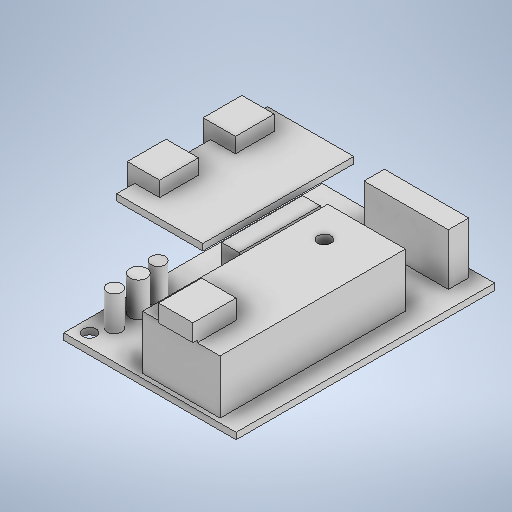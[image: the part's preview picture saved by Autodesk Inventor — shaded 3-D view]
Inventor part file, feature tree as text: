
AUTODESK INVENTOR PART (.ipt)
format: ipt  version: 2025.1 (Build 291241000, 241)  size: 356,864 bytes
history: native  units: mm
features: sketch x10, extrude x9, plane x2, hole x1
ambient origin geometry x8: Origin, YZ Plane, XZ Plane, XY Plane, X Axis, Y Axis, Z Axis, Center Point
bodies: Volumenkörper1 (feature_tree)
feature tree (22):
  extrude  "Extrusion1"  Depth=60.0mm
  extrude  "Extrusion2"  Depth=8.0mm
  extrude  "Extrusion3"  Depth=10.0mm
  plane  "Arbeitsebene1"
  extrude  "Extrusion4"  Depth=4.0mm
  extrude  "Extrusion5"  Depth=35.0mm
  extrude  "Extrusion6"  Depth=3.7mm
  extrude  "Extrusion7"  Depth=11.3mm
  extrude  "Extrusion8"  Depth=7.5mm
  extrude  "Extrusion9"  Depth=1.75mm
  plane  "Arbeitsebene2"
  hole  "Bohrung1"  [1 undecoded]
  sketch  "Skizze1"  dims[d0=40.0mm d1=60.0mm]
  sketch  "Skizze2"  dims[d2=1.5mm d3=0.0mm d4=8.0mm]
  sketch  "Skizze3"  dims[d5=10.0mm d6=10.0mm]
  sketch  "Skizze4"  dims[d7=17.0mm d8=0.0mm d9=4.0mm]
  sketch  "Skizze5"  dims[d10=1.0mm d11=0.0mm d12=35.0mm]
  sketch  "Skizze6"  dims[d13=20.0mm d14=3.7mm]
  sketch  "Skizze7"  dims[d15=29.0mm d16=11.3mm]
  sketch  "Skizze8"  dims[d17=1.5mm d18=0.0mm d19=7.5mm]
  sketch  "Skizze9"  dims[d20=9.0mm d21=1.75mm]
  sketch  "Skizze10"  dims[d22=4.2mm d23=4.2mm d24=9.0mm d25=3.5mm d26=1.5mm d27=0.0mm d28=0.0mm d29=18.0mm d30=43.0mm d31=4.7mm d32=12.5mm d33=0.0mm d34=8.0mm d35=0.0mm d36=12.0mm d37=0.0mm d38=12.0mm d39=0.0mm d40=3.0mm d41=3.0mm d42=16.0mm d43=36.5mm d44=3.1mm d45=6.0mm d46=4.0mm d47=2.0mm d48=90.0deg d49=11.8mm d50=0.0mm]
note: 1 required parameter value undecoded (feature->parameter linkage not recoverable at this tier; creation-order binding heuristic only, values carry confidence <= 0.55)
